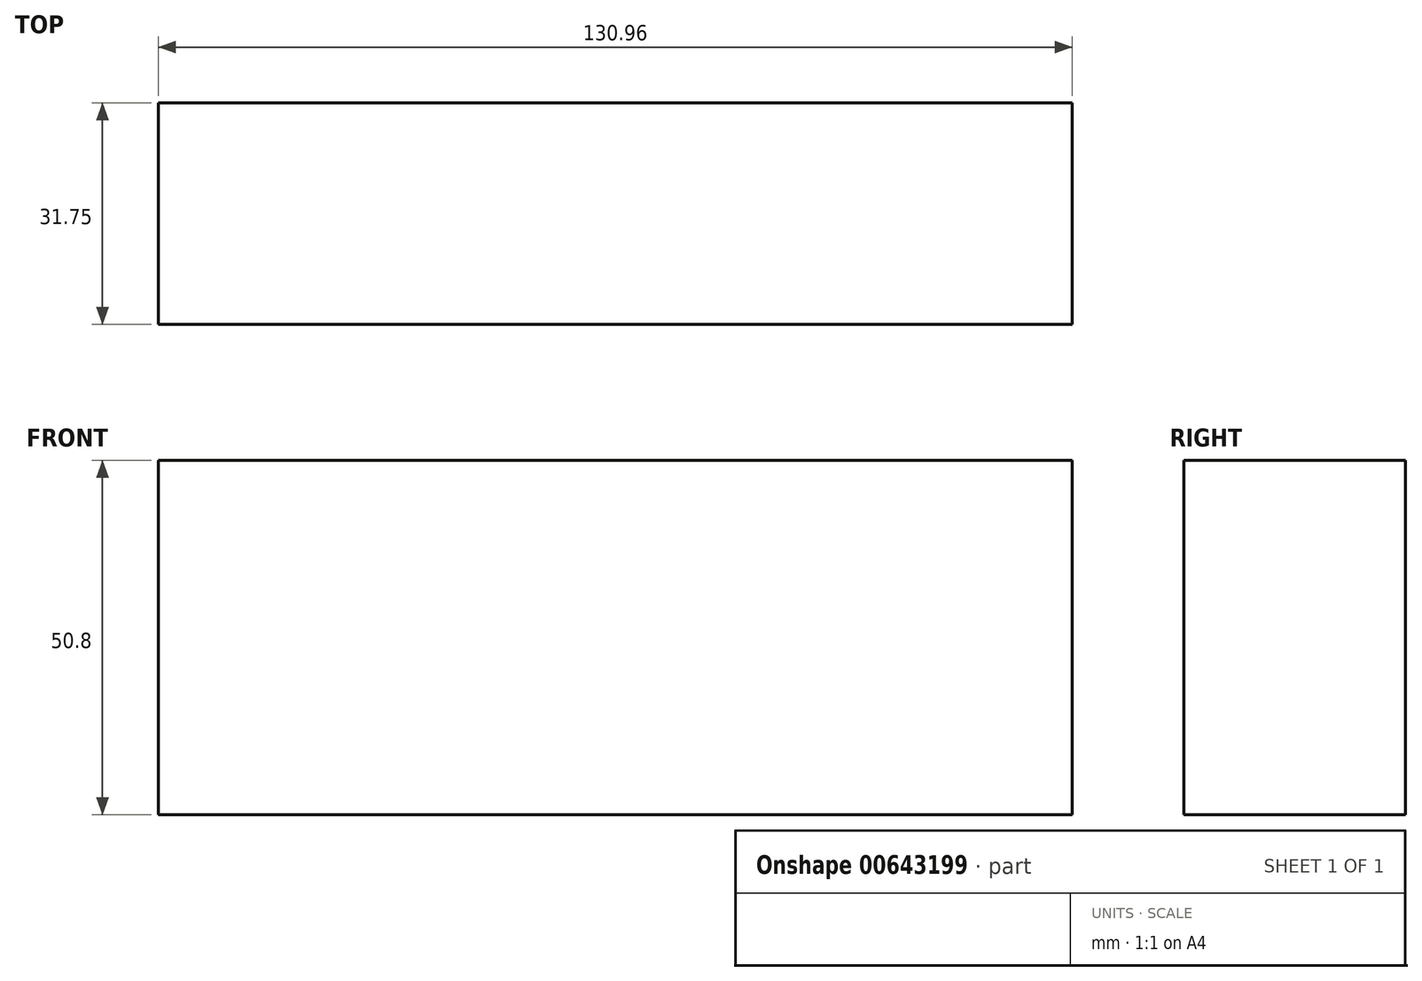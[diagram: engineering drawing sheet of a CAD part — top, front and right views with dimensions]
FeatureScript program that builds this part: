
annotation { "Feature Type Name" : "Feature", "Feature Type Description" : "" }
export const myFeature = defineFeature(function(context is Context, id is Id, definition is map)
    precondition{}
    {
        {
            var Q0;
            Q0=qCreatedBy(makeId("Right.planeOp"),FACE);
            var sketch = newSketch(context, id + "F0", { "sketchPlane" : qUnion([Q0])});
            skLineSegment(sketch, "E0.bottom", {"start": v(0, 2.15) * mm, "end": v(31.75, 2.15) * mm});
            skLineSegment(sketch, "E0.top", {"start": v(0, 52.95) * mm, "end": v(31.75, 52.95) * mm});
            skLineSegment(sketch, "E0.left", {"start": v(0, 2.15) * mm, "end": v(0, 52.95) * mm});
            skLineSegment(sketch, "E0.right", {"start": v(31.75, 2.15) * mm, "end": v(31.75, 52.95) * mm});
            skSolve(sketch);
        }
        {
            var Q0;
            Q0=qSketchRegion(id+"F0",true);
            extrude(context, id + "F1", {"entities" : qUnion([Q0]), "depth" : 130.96 * mm, "offsetDistance" : 25.4 * mm});
        }
    });
